# Revit family: LeeSti recessed adjustable trim 1' 2' 3' 4' Revit Family 06-09-2017
name_source: partatom
category: Lighting Fixtures
revit_build: Autodesk Revit 2014 (Build: 20130308_1515(x64)
units: mm (PartAtom-declared; Revit-internal decimal feet)

## types (4) — shared parameters
Color Filter = 16777215
Dimming Lamp Color Temperature Shift = <None>
Tilt Angle = 90.00°
finish = Metal, Paint Finish, White, Matte

## per-type parameters (varying)
| type | 1' flage | 2' flage | 3' flage | 4' flage | Emit from Line Length | Photometric Web File | Run | arraylight | lightnumber | singlelight |
| Leesti Adjustable Trim 2' | No | Yes | No | No | 1' - 11 1/4" | Leesti_twofeett_module_film.IES | 1' - 11 3/4" | Yes | 2 | No |
| Leesti Adjustable Trim 4' | No | No | No | Yes | 3' - 9 1/2" | Leesti_fourfeett_module_film.IES | 3' - 10" | Yes | 4 | No |
| Leesti Adjustable Trim 1' | Yes | No | No | No | 0' - 11 1/2" | Leesti_onefoot_module_film.IES | 1' - 0" | No | 2 | Yes |
| Leesti Adjustable Trim 3' | No | No | Yes | No | 2' - 10 1/2" | Leesti_fourfeett_module_film.IES | 2' - 11" | Yes | 3 | No |

## geometry (parser evidence)
native form markers: Sweep x2
no freeform markers — native parametric forms only
